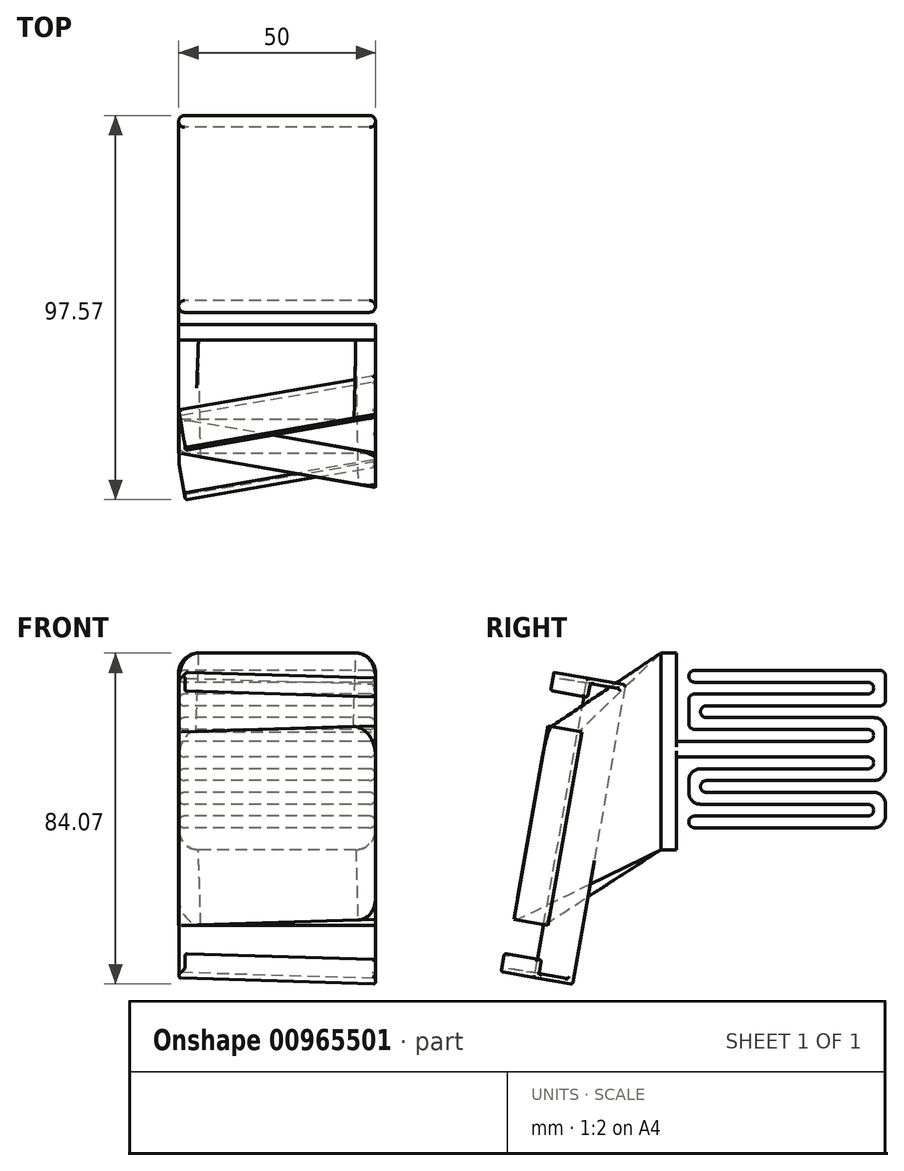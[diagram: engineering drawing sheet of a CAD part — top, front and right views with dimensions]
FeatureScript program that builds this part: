
annotation { "Feature Type Name" : "Feature", "Feature Type Description" : "" }
export const myFeature = defineFeature(function(context is Context, id is Id, definition is map)
    precondition{}
    {
        {
            var Q0;
            Q0=qCreatedBy(makeId("Right.planeOp"),FACE);
            var sketch = newSketch(context, id + "F0", { "sketchPlane" : qUnion([Q0])});
            skLineSegment(sketch, "E0", {"start": v(-23.52, 25) * mm, "end": v(-23.52, -25) * mm});
            skLineSegment(sketch, "E1", {"start": v(-23.52, -25) * mm, "end": v(-19.52, -25) * mm});
            skLineSegment(sketch, "E2", {"start": v(-19.52, -25) * mm, "end": v(-19.52, -1.4) * mm});
            skLineSegment(sketch, "E3", {"start": v(-19.52, -1.4) * mm, "end": v(29.06, -1.4) * mm});
            skLineSegment(sketch, "E4", {"start": v(-23.52, 25) * mm, "end": v(-19.52, 25) * mm});
            skLineSegment(sketch, "E5", {"start": v(-19.52, 25) * mm, "end": v(-19.52, 2.6) * mm});
            skLineSegment(sketch, "E6", {"start": v(-19.52, 2.6) * mm, "end": v(29.06, 2.6) * mm});
            skLineSegment(sketch, "E7", {"start": v(30.56, 4.1) * mm, "end": v(30.56, 4.1) * mm});
            skLineSegment(sketch, "E8", {"start": v(29.06, 5.6) * mm, "end": v(-14.94, 5.6) * mm});
            skLineSegment(sketch, "E9", {"start": v(-16.44, 7.1) * mm, "end": v(-16.44, 13.1) * mm});
            skLineSegment(sketch, "E10", {"start": v(-14.94, 14.6) * mm, "end": v(29.06, 14.6) * mm});
            skLineSegment(sketch, "E11", {"start": v(30.56, 16.1) * mm, "end": v(30.56, 16.1) * mm});
            skLineSegment(sketch, "E12", {"start": v(29.06, 17.6) * mm, "end": v(-14.94, 17.6) * mm});
            skLineSegment(sketch, "E13", {"start": v(-16.44, 19.1) * mm, "end": v(-16.44, 19.1) * mm});
            skLineSegment(sketch, "E14", {"start": v(-14.94, 20.6) * mm, "end": v(32.06, 20.6) * mm});
            skLineSegment(sketch, "E15", {"start": v(32.06, 11.6) * mm, "end": v(-11.94, 11.6) * mm});
            skLineSegment(sketch, "E16", {"start": v(-13.44, 10.1) * mm, "end": v(-13.44, 10.1) * mm});
            skLineSegment(sketch, "E17", {"start": v(-11.94, 8.6) * mm, "end": v(30.56, 8.6) * mm});
            skLineSegment(sketch, "E18", {"start": v(33.56, 5.6) * mm, "end": v(33.56, -4.4) * mm});
            skLineSegment(sketch, "E19", {"start": v(30.56, -2.9) * mm, "end": v(30.56, -2.9) * mm});
            skLineSegment(sketch, "E20", {"start": v(29.06, -4.4) * mm, "end": v(-13.44, -4.4) * mm});
            skLineSegment(sketch, "E21", {"start": v(-16.44, -7.4) * mm, "end": v(-16.44, -10.4) * mm});
            skLineSegment(sketch, "E22", {"start": v(-13.44, -13.4) * mm, "end": v(29.06, -13.4) * mm});
            skLineSegment(sketch, "E23", {"start": v(30.56, -14.9) * mm, "end": v(30.56, -14.9) * mm});
            skLineSegment(sketch, "E24", {"start": v(29.06, -16.4) * mm, "end": v(-14.94, -16.4) * mm});
            skLineSegment(sketch, "E25", {"start": v(-16.44, -17.9) * mm, "end": v(-16.44, -17.9) * mm});
            skLineSegment(sketch, "E26", {"start": v(-14.94, -19.4) * mm, "end": v(30.56, -19.4) * mm});
            skLineSegment(sketch, "E27", {"start": v(33.56, -16.4) * mm, "end": v(33.56, -13.4) * mm});
            skLineSegment(sketch, "E28", {"start": v(30.56, -10.4) * mm, "end": v(-11.94, -10.4) * mm});
            skLineSegment(sketch, "E29", {"start": v(-13.44, -8.9) * mm, "end": v(-13.44, -8.9) * mm});
            skLineSegment(sketch, "E30", {"start": v(-11.94, -7.4) * mm, "end": v(30.56, -7.4) * mm});
            skLineSegment(sketch, "E31", {"start": v(33.56, 13.1) * mm, "end": v(33.56, 19.1) * mm});
            skPoint(sketch, "E32.visualSharp", {"position": v(33.56, 20.6) * mm});
            skArc(sketch, "E32.filletArc", {"start": v(33.56, 19.1) * mm, "mid": v(33.12, 20.15) * mm, "end": v(32.06, 20.6) * mm});
            skPoint(sketch, "E33.visualSharp", {"position": v(30.56, 17.6) * mm});
            skArc(sketch, "E33.filletArc", {"start": v(30.56, 16.1) * mm, "mid": v(30.12, 17.15) * mm, "end": v(29.06, 17.6) * mm});
            skPoint(sketch, "E34.visualSharp", {"position": v(30.56, 14.6) * mm});
            skArc(sketch, "E34.filletArc", {"start": v(29.06, 14.6) * mm, "mid": v(30.12, 15.03) * mm, "end": v(30.56, 16.1) * mm});
            skPoint(sketch, "E35.visualSharp", {"position": v(33.56, 11.6) * mm});
            skArc(sketch, "E35.filletArc", {"start": v(32.06, 11.6) * mm, "mid": v(33.12, 12.03) * mm, "end": v(33.56, 13.1) * mm});
            skPoint(sketch, "E36.visualSharp", {"position": v(-16.44, 20.6) * mm});
            skArc(sketch, "E36.filletArc", {"start": v(-14.94, 20.6) * mm, "mid": v(-16, 20.15) * mm, "end": v(-16.44, 19.1) * mm});
            skPoint(sketch, "E37.visualSharp", {"position": v(-16.44, 17.6) * mm});
            skArc(sketch, "E37.filletArc", {"start": v(-16.44, 19.1) * mm, "mid": v(-16, 18.03) * mm, "end": v(-14.94, 17.6) * mm});
            skPoint(sketch, "E38.visualSharp", {"position": v(-16.44, 14.6) * mm});
            skArc(sketch, "E38.filletArc", {"start": v(-14.94, 14.6) * mm, "mid": v(-16, 14.15) * mm, "end": v(-16.44, 13.1) * mm});
            skPoint(sketch, "E39.visualSharp", {"position": v(-16.44, 5.6) * mm});
            skArc(sketch, "E39.filletArc", {"start": v(-16.44, 7.1) * mm, "mid": v(-16, 6.03) * mm, "end": v(-14.94, 5.6) * mm});
            skPoint(sketch, "E40.visualSharp", {"position": v(-13.44, 11.6) * mm});
            skArc(sketch, "E40.filletArc", {"start": v(-11.94, 11.6) * mm, "mid": v(-13, 11.15) * mm, "end": v(-13.44, 10.1) * mm});
            skPoint(sketch, "E41.visualSharp", {"position": v(-13.44, 8.6) * mm});
            skArc(sketch, "E41.filletArc", {"start": v(-13.44, 10.1) * mm, "mid": v(-13, 9.03) * mm, "end": v(-11.94, 8.6) * mm});
            skPoint(sketch, "E42.visualSharp", {"position": v(30.56, 5.6) * mm});
            skArc(sketch, "E42.filletArc", {"start": v(30.56, 4.1) * mm, "mid": v(30.12, 5.15) * mm, "end": v(29.06, 5.6) * mm});
            skPoint(sketch, "E43.visualSharp", {"position": v(30.56, 2.6) * mm});
            skArc(sketch, "E43.filletArc", {"start": v(29.06, 2.6) * mm, "mid": v(30.12, 3.03) * mm, "end": v(30.56, 4.1) * mm});
            skPoint(sketch, "E44.visualSharp", {"position": v(-13.44, -7.4) * mm});
            skArc(sketch, "E44.filletArc", {"start": v(-11.94, -7.4) * mm, "mid": v(-13, -7.85) * mm, "end": v(-13.44, -8.9) * mm});
            skPoint(sketch, "E45.visualSharp", {"position": v(-13.44, -10.4) * mm});
            skArc(sketch, "E45.filletArc", {"start": v(-13.44, -8.9) * mm, "mid": v(-13, -9.97) * mm, "end": v(-11.94, -10.4) * mm});
            skPoint(sketch, "E46.visualSharp", {"position": v(30.56, -13.4) * mm});
            skArc(sketch, "E46.filletArc", {"start": v(30.56, -14.9) * mm, "mid": v(30.12, -13.85) * mm, "end": v(29.06, -13.4) * mm});
            skPoint(sketch, "E47.visualSharp", {"position": v(30.56, -16.4) * mm});
            skArc(sketch, "E47.filletArc", {"start": v(29.06, -16.4) * mm, "mid": v(30.12, -15.97) * mm, "end": v(30.56, -14.9) * mm});
            skPoint(sketch, "E48.visualSharp", {"position": v(30.56, -4.4) * mm});
            skArc(sketch, "E48.filletArc", {"start": v(29.06, -4.4) * mm, "mid": v(30.12, -3.97) * mm, "end": v(30.56, -2.9) * mm});
            skPoint(sketch, "E49.visualSharp", {"position": v(30.56, -1.4) * mm});
            skArc(sketch, "E49.filletArc", {"start": v(30.56, -2.9) * mm, "mid": v(30.12, -1.85) * mm, "end": v(29.06, -1.4) * mm});
            skPoint(sketch, "E50.visualSharp", {"position": v(33.56, -19.4) * mm});
            skArc(sketch, "E50.filletArc", {"start": v(30.56, -19.4) * mm, "mid": v(32.68, -18.53) * mm, "end": v(33.56, -16.4) * mm});
            skPoint(sketch, "E51.visualSharp", {"position": v(33.56, -10.4) * mm});
            skArc(sketch, "E51.filletArc", {"start": v(33.56, -13.4) * mm, "mid": v(32.68, -11.29) * mm, "end": v(30.56, -10.4) * mm});
            skPoint(sketch, "E52.visualSharp", {"position": v(33.56, -7.4) * mm});
            skArc(sketch, "E52.filletArc", {"start": v(30.56, -7.4) * mm, "mid": v(32.68, -6.53) * mm, "end": v(33.56, -4.4) * mm});
            skPoint(sketch, "E53.visualSharp", {"position": v(33.56, 8.6) * mm});
            skArc(sketch, "E53.filletArc", {"start": v(33.56, 5.6) * mm, "mid": v(32.68, 7.71) * mm, "end": v(30.56, 8.6) * mm});
            skPoint(sketch, "E54.visualSharp", {"position": v(-16.44, -19.4) * mm});
            skArc(sketch, "E54.filletArc", {"start": v(-16.44, -17.9) * mm, "mid": v(-16, -18.97) * mm, "end": v(-14.94, -19.4) * mm});
            skPoint(sketch, "E55.visualSharp", {"position": v(-16.44, -16.4) * mm});
            skArc(sketch, "E55.filletArc", {"start": v(-14.94, -16.4) * mm, "mid": v(-16, -16.85) * mm, "end": v(-16.44, -17.9) * mm});
            skPoint(sketch, "E56.visualSharp", {"position": v(-16.44, -4.4) * mm});
            skArc(sketch, "E56.filletArc", {"start": v(-13.44, -4.4) * mm, "mid": v(-15.56, -5.29) * mm, "end": v(-16.44, -7.4) * mm});
            skPoint(sketch, "E57.visualSharp", {"position": v(-16.44, -13.4) * mm});
            skArc(sketch, "E57.filletArc", {"start": v(-16.44, -10.4) * mm, "mid": v(-15.56, -12.53) * mm, "end": v(-13.44, -13.4) * mm});
            skSolve(sketch);
        }
        {
            var Q0;
            Q0 = qSketchRegion(id + "F0", true);
            extrude(context, id + "F1", {"entities" : qUnion([Q0]), "depth" : 50 * mm, "offsetDistance" : 25 * mm});
        }
        {
            var Q0;
            Q0=qCreatedBy(makeId("Top.planeOp"),FACE);
            var sketch = newSketch(context, id + "F2", { "sketchPlane" : qUnion([Q0])});
            skLineSegment(sketch, "E58", {"start": v(0, -43.52) * mm, "end": v(50, -43.52) * mm});
            skLineSegment(sketch, "E59", {"start": v(50, -43.52) * mm, "end": v(50, -52.34) * mm});
            skLineSegment(sketch, "E60", {"start": v(50, -52.34) * mm, "end": v(0, -43.52) * mm});
            skSolve(sketch);
        }
        {
            var Q0;
            Q0=makeQuery(id+"F2.imprint","IMPRINT",FACE,{"disambiguationData":[TD([[makeQuery(id+"F2.imprint","IMPRINT",EDGE,{"derivedFrom":sQuery(id+"F2.wireOp",EDGE,"E58")}),-1.0]])]});
            extrude(context, id + "F3", {"entities" : qUnion([Q0]), "endBound" : BoundingType.SYMMETRIC, "depth" : 50 * mm, "offsetDistance" : 25 * mm});
        }
        {
            var Q0;
            Q0=makeQuery(id+"F3.opExtrude","SWEPT_BODY",BODY,{"disambiguationData":[OSD([sQuery(id+"F2.wireOp",EDGE,"E58"),sQuery(id+"F2.wireOp",EDGE,"E59"),sQuery(id+"F2.wireOp",EDGE,"E60")])]});
            var Q1;
            Q1=makeQuery(id+"F3.opExtrude","CAP_EDGE",EDGE,{"disambiguationData":[OSD([sQuery(id+"F2.wireOp",EDGE,"E58")])],"isStart":false});
            transform(context, id + "F4", {"entities" : qUnion([Q0]), "transformType" : TransformType.ROTATION, "transformAxis" : qUnion([Q1]), "angle" : 10 * degree, "oppositeDirection" : true, "makeCopy" : false});
        }
        {
            var Q0;
            Q0=makeQuery(id+"F3.opExtrude","SWEPT_BODY",BODY,{"disambiguationData":[OSD([sQuery(id+"F2.wireOp",EDGE,"E58"),sQuery(id+"F2.wireOp",EDGE,"E59"),sQuery(id+"F2.wireOp",EDGE,"E60")])]});
            transform(context, id + "F5", {"entities" : qUnion([Q0]), "transformType" : TransformType.TRANSLATION_3D, "dx" : 0 * mm, "dy" : 0 * mm, "dz" : -20 * mm, "makeCopy" : false});
        }
        {
            var Q0;
            Q0=makeQuery(id+"F3.opExtrude","SWEPT_FACE",FACE,{"disambiguationData":[OSD([sQuery(id+"F2.wireOp",EDGE,"E60")])]});
            var Q1;
            Q1=makeQuery(id+"F1.opExtrude","SWEPT_FACE",FACE,{"disambiguationData":[OSD([sQuery(id+"F0.wireOp",EDGE,"E0")])]});
            loft(context, id + "F6", {"sheetProfilesArray" : [{ "sheetProfileEntities" : qUnion([Q0]) }, { "sheetProfileEntities" : qUnion([Q1]) }]});
        }
        {
            var Q0;
            Q0=makeQuery(id+"F6.opLoft","SWEPT_FACE",FACE,{"disambiguationData":[OSD([sQuery(id+"F0.wireOp",EDGE,"E0"),sQuery(id+"F0.wireOp",EDGE,"E1"),sQuery(id+"F0.wireOp",EDGE,"E4"),sQuery(id+"F2.wireOp",EDGE,"E58"),sQuery(id+"F2.wireOp",EDGE,"E60")])]});
            var sketch = newSketch(context, id + "F7", { "sketchPlane" : qUnion([Q0])});
            skLineSegment(sketch, "E61", {"start": v(43.52, 5) * mm, "end": v(41.16, 18.4) * mm});
            skLineSegment(sketch, "E62", {"start": v(52.2, -44.24) * mm, "end": v(54.56, -57.63) * mm});
            skLineSegment(sketch, "E63", {"start": v(41.16, 18.4) * mm, "end": v(50.9, 20.11) * mm});
            skLineSegment(sketch, "E64", {"start": v(54.56, -57.63) * mm, "end": v(64.31, -55.91) * mm});
            skLineSegment(sketch, "E65", {"start": v(50.9, 20.11) * mm, "end": v(51.72, 15.48) * mm});
            skLineSegment(sketch, "E66", {"start": v(42.55, 17.42) * mm, "end": v(55.54, -56.24) * mm});
            skLineSegment(sketch, "E67", {"start": v(63.5, -51.29) * mm, "end": v(64.31, -55.91) * mm});
            skLineSegment(sketch, "E68", {"start": v(51.72, 15.48) * mm, "end": v(50.54, 15.28) * mm});
            skLineSegment(sketch, "E69", {"start": v(50.54, 15.28) * mm, "end": v(49.94, 18.72) * mm});
            skLineSegment(sketch, "E70", {"start": v(49.94, 18.72) * mm, "end": v(42.55, 17.42) * mm});
            skLineSegment(sketch, "E71", {"start": v(63.5, -51.29) * mm, "end": v(62.32, -51.5) * mm});
            skLineSegment(sketch, "E72", {"start": v(62.32, -51.5) * mm, "end": v(62.92, -54.94) * mm});
            skLineSegment(sketch, "E73", {"start": v(62.92, -54.94) * mm, "end": v(55.54, -56.24) * mm});
            skSolve(sketch);
        }
        {
            var Q0;
            Q0=makeQuery(id+"F7.imprint","IMPRINT",FACE,{"disambiguationData":[TD([[makeQuery(id+"F7.imprint","IMPRINT",EDGE,{"derivedFrom":sQuery(id+"F7.wireOp",EDGE,"E61")}),-1.0]])]});
            extrude(context, id + "F8", {"entities" : qUnion([Q0]), "oppositeDirection" : true, "depth" : 55 * mm, "offsetDistance" : 25 * mm});
        }
        {
            var Q0;
            Q0=makeQuery(id+"F8.opExtrude","SWEPT_BODY",BODY,{"disambiguationData":[OSD([sQuery(id+"F2.wireOp",EDGE,"E58"),sQuery(id+"F2.wireOp",EDGE,"E60"),sQuery(id+"F7.wireOp",EDGE,"E61"),sQuery(id+"F7.wireOp",EDGE,"E62"),sQuery(id+"F7.wireOp",EDGE,"E63"),sQuery(id+"F7.wireOp",EDGE,"E64"),sQuery(id+"F7.wireOp",EDGE,"E65"),sQuery(id+"F7.wireOp",EDGE,"E66"),sQuery(id+"F7.wireOp",EDGE,"E67"),sQuery(id+"F7.wireOp",EDGE,"E68"),sQuery(id+"F7.wireOp",EDGE,"E69"),sQuery(id+"F7.wireOp",EDGE,"E70"),sQuery(id+"F7.wireOp",EDGE,"E71"),sQuery(id+"F7.wireOp",EDGE,"E72"),sQuery(id+"F7.wireOp",EDGE,"E73")])]});
            var Q1;
            Q1=makeQuery(id+"F8.opExtrude","CAP_EDGE",EDGE,{"disambiguationData":[OSD([sQuery(id+"F2.wireOp",EDGE,"E58"),sQuery(id+"F2.wireOp",EDGE,"E60"),sQuery(id+"F7.wireOp",EDGE,"E61"),sQuery(id+"F7.wireOp",EDGE,"E62")])],"isStart":true});
            transform(context, id + "F9", {"entities" : qUnion([Q0]), "transformType" : TransformType.ROTATION, "transformAxis" : qUnion([Q1]), "angle" : 10 * degree, "makeCopy" : false});
        }
        {
            var Q0;
            Q0=makeQuery(id+"F8.opExtrude","SWEPT_EDGE",EDGE,{"disambiguationData":[OSD([sQuery(id+"F7.wireOp",EDGE,"E72"),sQuery(id+"F7.wireOp",EDGE,"E73")])]});
            var Q1;
            Q1=makeQuery(id+"F8.opExtrude","SWEPT_EDGE",EDGE,{"disambiguationData":[OSD([sQuery(id+"F7.wireOp",EDGE,"E66"),sQuery(id+"F7.wireOp",EDGE,"E73")])]});
            var Q2;
            Q2=makeQuery(id+"F8.opExtrude","SWEPT_EDGE",EDGE,{"disambiguationData":[OSD([sQuery(id+"F7.wireOp",EDGE,"E69"),sQuery(id+"F7.wireOp",EDGE,"E70")])]});
            var Q3;
            Q3=makeQuery(id+"F8.opExtrude","SWEPT_EDGE",EDGE,{"disambiguationData":[OSD([sQuery(id+"F7.wireOp",EDGE,"E66"),sQuery(id+"F7.wireOp",EDGE,"E70")])]});
            var Q4;
            Q4=makeQuery(id+"F8.opExtrude","SWEPT_EDGE",EDGE,{"disambiguationData":[OSD([sQuery(id+"F7.wireOp",EDGE,"E68"),sQuery(id+"F7.wireOp",EDGE,"E69")])]});
            var Q5;
            Q5=makeQuery(id+"F8.opExtrude","SWEPT_EDGE",EDGE,{"disambiguationData":[OSD([sQuery(id+"F7.wireOp",EDGE,"E65"),sQuery(id+"F7.wireOp",EDGE,"E68")])]});
            var Q6;
            Q6=makeQuery(id+"F8.opExtrude","SWEPT_EDGE",EDGE,{"disambiguationData":[OSD([sQuery(id+"F7.wireOp",EDGE,"E71"),sQuery(id+"F7.wireOp",EDGE,"E72")])]});
            var Q7;
            Q7=makeQuery(id+"F8.opExtrude","SWEPT_EDGE",EDGE,{"disambiguationData":[OSD([sQuery(id+"F7.wireOp",EDGE,"E67"),sQuery(id+"F7.wireOp",EDGE,"E71")])]});
            var Q8;
            Q8=makeQuery(id+"F8.opExtrude","SWEPT_EDGE",EDGE,{"disambiguationData":[OSD([sQuery(id+"F7.wireOp",EDGE,"E64"),sQuery(id+"F7.wireOp",EDGE,"E67")])]});
            var Q9;
            Q9=makeQuery(id+"F8.opExtrude","SWEPT_EDGE",EDGE,{"disambiguationData":[OSD([sQuery(id+"F7.wireOp",EDGE,"E62"),sQuery(id+"F7.wireOp",EDGE,"E64")])]});
            var Q10;
            Q10=makeQuery(id+"F8.opExtrude","SWEPT_EDGE",EDGE,{"disambiguationData":[OSD([sQuery(id+"F7.wireOp",EDGE,"E61"),sQuery(id+"F7.wireOp",EDGE,"E63")])]});
            fillet(context, id + "F10", {"entities" : qUnion([Q0, Q1, Q2, Q3, Q4, Q5, Q6, Q7, Q8, Q9, Q10]), "radius" : 0.5 * mm, "tangentPropagation" : true, "allowEdgeOverflow" : false});
        }
        {
            var Q0;
            Q0=makeQuery(id+"F8.opExtrude","CAP_EDGE",EDGE,{"disambiguationData":[OSD([sQuery(id+"F7.wireOp",EDGE,"E66")])],"isStart":false});
            var Q1;
            Q1=makeQuery(id+"F8.opExtrude","CAP_EDGE",EDGE,{"disambiguationData":[OSD([sQuery(id+"F7.wireOp",EDGE,"E73")])],"isStart":false});
            var Q2;
            Q2=makeQuery(id+"F8.opExtrude","CAP_EDGE",EDGE,{"disambiguationData":[OSD([sQuery(id+"F7.wireOp",EDGE,"E72")])],"isStart":false});
            var Q3;
            Q3=makeQuery(id+"F8.opExtrude","CAP_EDGE",EDGE,{"disambiguationData":[OSD([sQuery(id+"F7.wireOp",EDGE,"E69")])],"isStart":false});
            var Q4;
            Q4=makeQuery(id+"F8.opExtrude","CAP_EDGE",EDGE,{"disambiguationData":[OSD([sQuery(id+"F7.wireOp",EDGE,"E70")])],"isStart":false});
            fillet(context, id + "F11", {"entities" : qUnion([Q0, Q1, Q2, Q3, Q4]), "radius" : 0.5 * mm, "tangentPropagation" : true, "allowEdgeOverflow" : false});
        }
        {
            var Q0;
            Q0=makeQuery(id+"F8.opExtrude","CAP_EDGE",EDGE,{"disambiguationData":[OSD([sQuery(id+"F7.wireOp",EDGE,"E69")])],"isStart":true});
            var Q1;
            Q1=makeQuery(id+"F8.opExtrude","CAP_EDGE",EDGE,{"disambiguationData":[OSD([sQuery(id+"F7.wireOp",EDGE,"E70")])],"isStart":true});
            var Q2;
            Q2=makeQuery(id+"F8.opExtrude","CAP_EDGE",EDGE,{"disambiguationData":[OSD([sQuery(id+"F7.wireOp",EDGE,"E66")])],"isStart":true});
            fillet(context, id + "F12", {"entities" : qUnion([Q0, Q1, Q2]), "radius" : 0.5 * mm, "tangentPropagation" : true, "allowEdgeOverflow" : false});
        }
        {
            var Q0;
            Q0=makeQuery(id+"F6.opLoft","SWEPT_EDGE",EDGE,{"disambiguationData":[OSD([sQuery(id+"F0.wireOp",EDGE,"E0"),sQuery(id+"F0.wireOp",EDGE,"E1"),sQuery(id+"F2.wireOp",EDGE,"E59"),sQuery(id+"F2.wireOp",EDGE,"E60")])]});
            var Q1;
            Q1=makeQuery(id+"F6.opLoft","SWEPT_EDGE",EDGE,{"disambiguationData":[OSD([sQuery(id+"F0.wireOp",EDGE,"E0"),sQuery(id+"F0.wireOp",EDGE,"E1"),sQuery(id+"F2.wireOp",EDGE,"E58"),sQuery(id+"F2.wireOp",EDGE,"E60")])]});
            var Q2;
            Q2=makeQuery(id+"F6.opLoft","SWEPT_EDGE",EDGE,{"disambiguationData":[OSD([sQuery(id+"F0.wireOp",EDGE,"E0"),sQuery(id+"F0.wireOp",EDGE,"E4"),sQuery(id+"F2.wireOp",EDGE,"E58"),sQuery(id+"F2.wireOp",EDGE,"E60")])]});
            var Q3;
            Q3=makeQuery(id+"F6.opLoft","SWEPT_EDGE",EDGE,{"disambiguationData":[OSD([sQuery(id+"F0.wireOp",EDGE,"E0"),sQuery(id+"F0.wireOp",EDGE,"E4"),sQuery(id+"F2.wireOp",EDGE,"E59"),sQuery(id+"F2.wireOp",EDGE,"E60")])]});
            fillet(context, id + "F13", {"entities" : qUnion([Q0, Q1, Q2, Q3]), "radius" : 5 * mm, "tangentPropagation" : true, "allowEdgeOverflow" : false});
        }
        {
            var Q0;
            Q0=makeQuery(id+"F1.opExtrude","CAP_EDGE",EDGE,{"disambiguationData":[OSD([sQuery(id+"F0.wireOp",EDGE,"E1")])],"isStart":false});
            var Q1;
            Q1=makeQuery(id+"F1.opExtrude","CAP_EDGE",EDGE,{"disambiguationData":[OSD([sQuery(id+"F0.wireOp",EDGE,"E1")])],"isStart":true});
            var Q2;
            Q2=makeQuery(id+"F1.opExtrude","CAP_EDGE",EDGE,{"disambiguationData":[OSD([sQuery(id+"F0.wireOp",EDGE,"E4")])],"isStart":true});
            var Q3;
            Q3=makeQuery(id+"F1.opExtrude","CAP_EDGE",EDGE,{"disambiguationData":[OSD([sQuery(id+"F0.wireOp",EDGE,"E4")])],"isStart":false});
            fillet(context, id + "F14", {"entities" : qUnion([Q0, Q1, Q2, Q3]), "radius" : 5 * mm, "tangentPropagation" : true, "allowEdgeOverflow" : false});
        }
        {
            var Q0;
            Q0=makeQuery(id+"F1.opExtrude","CAP_EDGE",EDGE,{"disambiguationData":[OSD([sQuery(id+"F0.wireOp",EDGE,"E26")])],"isStart":false});
            var Q1;
            Q1=makeQuery(id+"F1.opExtrude","CAP_EDGE",EDGE,{"disambiguationData":[OSD([sQuery(id+"F0.wireOp",EDGE,"E26")])],"isStart":true});
            var Q2;
            Q2=makeQuery(id+"F1.opExtrude","CAP_EDGE",EDGE,{"disambiguationData":[OSD([sQuery(id+"F0.wireOp",EDGE,"E14")])],"isStart":true});
            var Q3;
            Q3=makeQuery(id+"F1.opExtrude","CAP_EDGE",EDGE,{"disambiguationData":[OSD([sQuery(id+"F0.wireOp",EDGE,"E14")])],"isStart":false});
            fillet(context, id + "F15", {"entities" : qUnion([Q0, Q1, Q2, Q3]), "radius" : 1.5 * mm, "tangentPropagation" : true, "allowEdgeOverflow" : false});
        }
        {
            var Q0;
            Q0=makeQuery(id+"F1.opExtrude","SWEPT_FACE",FACE,{"disambiguationData":[OSD([sQuery(id+"F0.wireOp",EDGE,"E5")])]});
            var sketch = newSketch(context, id + "F16", { "sketchPlane" : qUnion([Q0])});
            skLineSegment(sketch, "E74", {"start": v(-50, 20) * mm, "end": v(-50, -117.96) * mm});
            skLineSegment(sketch, "E75", {"start": v(-50, 20) * mm, "end": v(-50, 120.94) * mm});
            skLineSegment(sketch, "E76", {"start": v(-50, 120.94) * mm, "end": v(-82.91, 120.94) * mm});
            skLineSegment(sketch, "E77", {"start": v(-82.91, 120.94) * mm, "end": v(-99.06, -136.34) * mm});
            skLineSegment(sketch, "E78", {"start": v(-99.06, -136.34) * mm, "end": v(-50, -117.96) * mm});
            skSolve(sketch);
        }
        {
            var Q0;
            {var subQ0=sQuery(id+"F16.wireOp",EDGE,"E75");Q0=makeQuery(id+"F16.imprint","IMPRINT",FACE,{"disambiguationData":[TD([[makeQuery(id+"F16.imprint","IMPRINT",EDGE,{"derivedFrom":subQ0}),1.0]])]});}
            extrude(context, id + "F17", {"entities" : qUnion([Q0]), "operationType" : NewBodyOperationType.REMOVE, "oppositeDirection" : true, "depth" : 100 * mm, "offsetDistance" : 25 * mm});
        }
        {
            var Q0;
            Q0=makeQuery(id+"F17.boolean.opBoolean","INTERSECT",EDGE,{"derivedFrom":[makeQuery(id+"F8.opExtrude","SWEPT_FACE",FACE,{"disambiguationData":[OSD([sQuery(id+"F7.wireOp",EDGE,"E69")])]}),makeQuery(id+"F17.opExtrude","SWEPT_FACE",FACE,{"disambiguationData":[OSD([sQuery(id+"F16.wireOp",EDGE,"E74"),sQuery(id+"F16.wireOp",EDGE,"E75")])]})]});
            var Q1;
            Q1=makeQuery(id+"F17.boolean.opBoolean","INTERSECT",EDGE,{"derivedFrom":[makeQuery(id+"F8.opExtrude","SWEPT_FACE",FACE,{"disambiguationData":[OSD([sQuery(id+"F7.wireOp",EDGE,"E70")])]}),makeQuery(id+"F17.opExtrude","SWEPT_FACE",FACE,{"disambiguationData":[OSD([sQuery(id+"F16.wireOp",EDGE,"E74"),sQuery(id+"F16.wireOp",EDGE,"E75")])]})]});
            var Q2;
            Q2=makeQuery(id+"F17.boolean.opBoolean","INTERSECT",EDGE,{"derivedFrom":[makeQuery(id+"F8.opExtrude","SWEPT_FACE",FACE,{"disambiguationData":[OSD([sQuery(id+"F7.wireOp",EDGE,"E63")])]}),makeQuery(id+"F17.opExtrude","SWEPT_FACE",FACE,{"disambiguationData":[OSD([sQuery(id+"F16.wireOp",EDGE,"E74"),sQuery(id+"F16.wireOp",EDGE,"E75")])]})]});
            var Q3;
            Q3=makeQuery(id+"F17.boolean.opBoolean","INTERSECT",EDGE,{"derivedFrom":[makeQuery(id+"F8.opExtrude","SWEPT_FACE",FACE,{"disambiguationData":[OSD([sQuery(id+"F7.wireOp",EDGE,"E65")])]}),makeQuery(id+"F17.opExtrude","SWEPT_FACE",FACE,{"disambiguationData":[OSD([sQuery(id+"F16.wireOp",EDGE,"E74"),sQuery(id+"F16.wireOp",EDGE,"E75")])]})]});
            var Q4;
            Q4=makeQuery(id+"F17.boolean.opBoolean","INTERSECT",EDGE,{"disambiguationData":[OD(0.0)],"derivedFrom":[makeQuery(id+"F8.opExtrude","SWEPT_FACE",FACE,{"disambiguationData":[OSD([sQuery(id+"F2.wireOp",EDGE,"E58"),sQuery(id+"F2.wireOp",EDGE,"E60"),sQuery(id+"F7.wireOp",EDGE,"E61"),sQuery(id+"F7.wireOp",EDGE,"E62")])]}),makeQuery(id+"F17.opExtrude","SWEPT_FACE",FACE,{"disambiguationData":[OSD([sQuery(id+"F16.wireOp",EDGE,"E74"),sQuery(id+"F16.wireOp",EDGE,"E75")])]})]});
            var Q5;
            Q5=makeQuery(id+"F17.boolean.opBoolean","INTERSECT",EDGE,{"derivedFrom":[makeQuery(id+"F8.opExtrude","SWEPT_FACE",FACE,{"disambiguationData":[OSD([sQuery(id+"F7.wireOp",EDGE,"E66")])]}),makeQuery(id+"F17.opExtrude","SWEPT_FACE",FACE,{"disambiguationData":[OSD([sQuery(id+"F16.wireOp",EDGE,"E74"),sQuery(id+"F16.wireOp",EDGE,"E75")])]})]});
            var Q6;
            Q6=makeQuery(id+"F17.boolean.opBoolean","INTERSECT",EDGE,{"disambiguationData":[OD(1.0)],"derivedFrom":[makeQuery(id+"F8.opExtrude","SWEPT_FACE",FACE,{"disambiguationData":[OSD([sQuery(id+"F2.wireOp",EDGE,"E58"),sQuery(id+"F2.wireOp",EDGE,"E60"),sQuery(id+"F7.wireOp",EDGE,"E61"),sQuery(id+"F7.wireOp",EDGE,"E62")])]}),makeQuery(id+"F17.opExtrude","SWEPT_FACE",FACE,{"disambiguationData":[OSD([sQuery(id+"F16.wireOp",EDGE,"E74"),sQuery(id+"F16.wireOp",EDGE,"E75")])]})]});
            var Q7;
            Q7=makeQuery(id+"F17.boolean.opBoolean","INTERSECT",EDGE,{"derivedFrom":[makeQuery(id+"F8.opExtrude","SWEPT_FACE",FACE,{"disambiguationData":[OSD([sQuery(id+"F7.wireOp",EDGE,"E64")])]}),makeQuery(id+"F17.opExtrude","SWEPT_FACE",FACE,{"disambiguationData":[OSD([sQuery(id+"F16.wireOp",EDGE,"E74"),sQuery(id+"F16.wireOp",EDGE,"E75")])]})]});
            var Q8;
            Q8=makeQuery(id+"F17.boolean.opBoolean","INTERSECT",EDGE,{"derivedFrom":[makeQuery(id+"F8.opExtrude","SWEPT_FACE",FACE,{"disambiguationData":[OSD([sQuery(id+"F7.wireOp",EDGE,"E73")])]}),makeQuery(id+"F17.opExtrude","SWEPT_FACE",FACE,{"disambiguationData":[OSD([sQuery(id+"F16.wireOp",EDGE,"E74"),sQuery(id+"F16.wireOp",EDGE,"E75")])]})]});
            var Q9;
            Q9=makeQuery(id+"F17.boolean.opBoolean","INTERSECT",EDGE,{"derivedFrom":[makeQuery(id+"F8.opExtrude","SWEPT_FACE",FACE,{"disambiguationData":[OSD([sQuery(id+"F7.wireOp",EDGE,"E67")])]}),makeQuery(id+"F17.opExtrude","SWEPT_FACE",FACE,{"disambiguationData":[OSD([sQuery(id+"F16.wireOp",EDGE,"E74"),sQuery(id+"F16.wireOp",EDGE,"E75")])]})]});
            fillet(context, id + "F18", {"entities" : qUnion([Q0, Q1, Q2, Q3, Q4, Q5, Q6, Q7, Q8, Q9]), "radius" : 0.5 * mm, "tangentPropagation" : true, "allowEdgeOverflow" : false});
        }
    });
